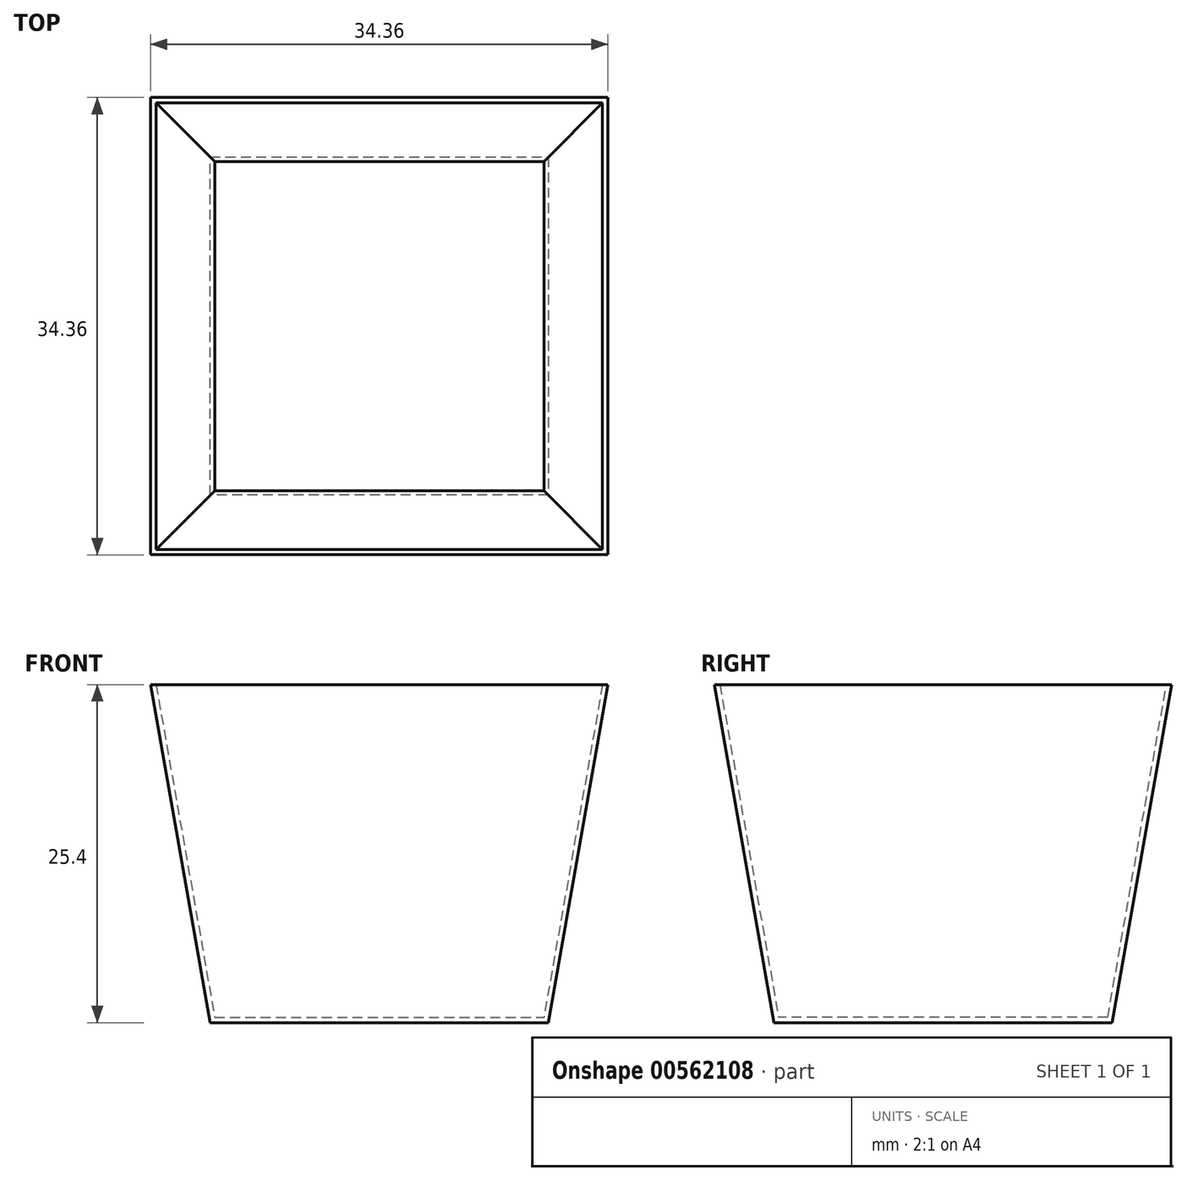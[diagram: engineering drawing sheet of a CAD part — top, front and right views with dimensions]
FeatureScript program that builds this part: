
annotation { "Feature Type Name" : "Feature", "Feature Type Description" : "" }
export const myFeature = defineFeature(function(context is Context, id is Id, definition is map)
    precondition{}
    {
        {
            var Q0;
            Q0=qCreatedBy(makeId("Top.planeOp"),FACE);
            var sketch = newSketch(context, id + "F0", { "sketchPlane" : qUnion([Q0])});
            skLineSegment(sketch, "E0.bottom", {"start": v(12.7, 12.7) * mm, "end": v(-12.7, 12.7) * mm});
            skLineSegment(sketch, "E0.top", {"start": v(12.7, -12.7) * mm, "end": v(-12.7, -12.7) * mm});
            skLineSegment(sketch, "E0.left", {"start": v(12.7, 12.7) * mm, "end": v(12.7, -12.7) * mm});
            skLineSegment(sketch, "E0.right", {"start": v(-12.7, 12.7) * mm, "end": v(-12.7, -12.7) * mm});
            skPoint(sketch, "E0.middle", {"position": v(0, 0) * mm});
            skSolve(sketch);
        }
        {
            var Q0;
            Q0 = qSketchRegion(id + "F0", true);
            extrude(context, id + "F1", {"entities" : qUnion([Q0]), "depth" : 25.4 * mm, "offsetDistance" : 25.4 * mm, "hasDraft" : true, "draftAngle" : 10 * degree});
        }
        {
            var Q0;
            Q0=makeQuery(id+"F1.opExtrude","CAP_FACE",FACE,{"disambiguationData":[OSD([sQuery(id+"F0.wireOp",EDGE,"E0.bottom"),sQuery(id+"F0.wireOp",EDGE,"E0.top"),sQuery(id+"F0.wireOp",EDGE,"E0.left"),sQuery(id+"F0.wireOp",EDGE,"E0.right")])],"isStart":false});
            shell(context, id + "F2", {"entities" : qUnion([Q0]), "thickness" : .4 * mm});
        }
    });
